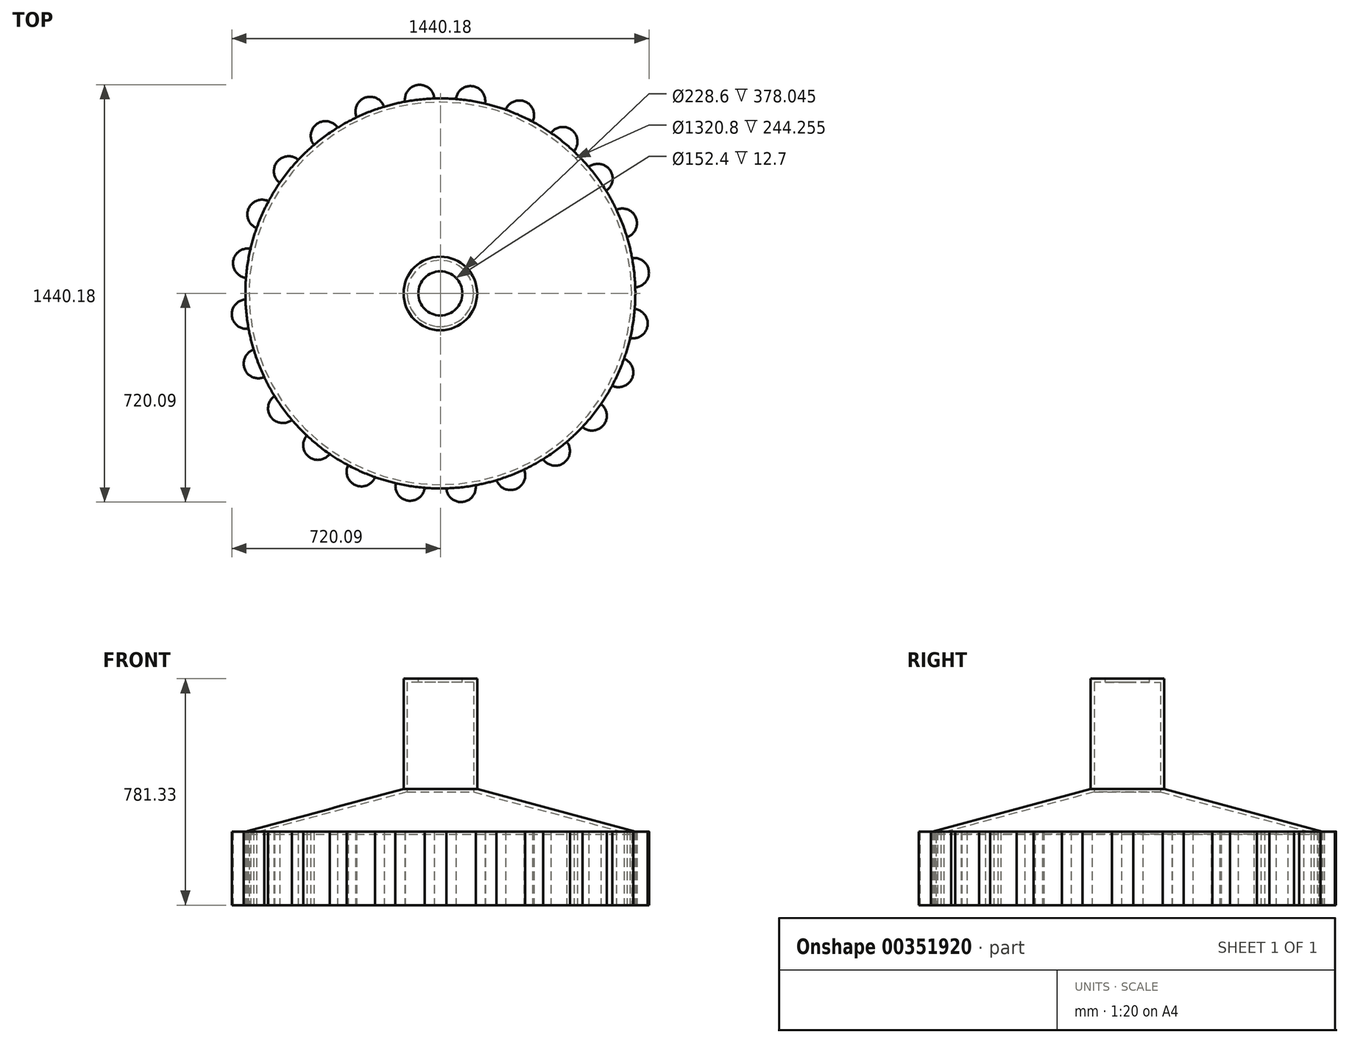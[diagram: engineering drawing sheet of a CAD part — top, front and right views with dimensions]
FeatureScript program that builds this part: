
annotation { "Feature Type Name" : "Feature", "Feature Type Description" : "" }
export const myFeature = defineFeature(function(context is Context, id is Id, definition is map)
    precondition{}
    {
        {
            var Q0;
            Q0=qCreatedBy(makeId("Front.planeOp"),FACE);
            var sketch = newSketch(context, id + "F0", { "sketchPlane" : qUnion([Q0])});
            skLineSegment(sketch, "E0", {"start": v(0, 0) * mm, "end": v(-673.1, 0) * mm});
            skLineSegment(sketch, "E1", {"start": v(-673.1, 0) * mm, "end": v(-673.1, 254) * mm});
            skLineSegment(sketch, "E2", {"start": v(-673.1, 254) * mm, "end": v(-127, 400.33) * mm});
            skPoint(sketch, "E3.center", {"position": v(0, 0) * mm});
            skLineSegment(sketch, "E4", {"start": v(0, 0) * mm, "end": v(0, 1146.38) * mm, "construction": true});
            skLineSegment(sketch, "E5", {"start": v(0, 0) * mm, "end": v(0, 781.33) * mm});
            skLineSegment(sketch, "E6", {"start": v(-127, 781.33) * mm, "end": v(0, 781.33) * mm});
            skLineSegment(sketch, "E7", {"start": v(-127, 400.33) * mm, "end": v(-127, 781.33) * mm});
            skSolve(sketch);
        }
        {
            var Q0;
            Q0=makeQuery(id+"F0.imprint","IMPRINT",FACE,{"disambiguationData":[TD([[makeQuery(id+"F0.imprint","IMPRINT",EDGE,{"derivedFrom":sQuery(id+"F0.wireOp",EDGE,"E0")}),-1.0]])]});
            var Q1;
            Q1=sQuery(id+"F0.wireOp",EDGE,"E4");
            revolve(context, id + "F1", {"entities" : qUnion([Q0]), "axis" : qUnion([Q1]), "revolveType" : RevolveType.FULL});
        }
        {
            var Q0;
            Q0=makeQuery(id+"F1.opRevolve","SWEPT_FACE",FACE,{"disambiguationData":[OSD([sQuery(id+"F0.wireOp",EDGE,"E0")])]});
            shell(context, id + "F2", {"entities" : qUnion([Q0]), "thickness" : 12.7 * mm});
        }
        {
            var Q0;
            Q0=makeQuery(id+"F1.opRevolve","SWEPT_FACE",FACE,{"disambiguationData":[OSD([sQuery(id+"F0.wireOp",EDGE,"E6")])]});
            var sketch = newSketch(context, id + "F3", { "sketchPlane" : qUnion([Q0])});
            skCircle(sketch, "E8", {"center": v(0, 0) * mm, "radius": 76.2 * mm});
            skSolve(sketch);
        }
        {
            var Q0;
            Q0=qSketchRegion(id+"F3",true);
            extrude(context, id + "F4", {"entities" : qUnion([Q0]), "operationType" : NewBodyOperationType.REMOVE, "endBound" : BoundingType.THROUGH_ALL, "oppositeDirection" : true, "depth" : 25.4 * mm});
        }
        {
            var Q0;
            Q0=makeQuery(id+"F1.opRevolve","SWEPT_FACE",FACE,{"disambiguationData":[OSD([sQuery(id+"F0.wireOp",EDGE,"E0")])]});
            var sketch = newSketch(context, id + "F5", { "sketchPlane" : qUnion([Q0])});
            skArc(sketch, "E9", {"start": v(-607.93, 288.94) * mm, "mid": v(-675.38, 260.55) * mm, "end": v(-644.47, 194.22) * mm});
            skArc(sketch, "E10", {"start": v(-607.93, 288.94) * mm, "mid": v(-627.99, 242.27) * mm, "end": v(-644.47, 194.22) * mm});
            skSolve(sketch);
        }
        {
            var Q0;
            Q0=makeQuery(id+"F5.imprint","IMPRINT",FACE,{"disambiguationData":[TD([[makeQuery(id+"F5.imprint","IMPRINT",EDGE,{"derivedFrom":sQuery(id+"F5.wireOp",EDGE,"E9")}),1.0]])]});
            extrude(context, id + "F6", {"entities" : qUnion([Q0]), "oppositeDirection" : true, "depth" : 254 * mm});
        }
        {
            var Q0;
            Q0=makeQuery(id+"F6.opExtrude","SWEPT_BODY",BODY,{"disambiguationData":[OSD([sQuery(id+"F5.wireOp",EDGE,"E9"),sQuery(id+"F5.wireOp",EDGE,"E10")])]});
            var Q1;
            Q1=makeQuery(id+"F4.boolean.opBoolean","INTERSECT",EDGE,{"derivedFrom":[makeQuery(id+"F2.opShell","OFFSET_FACE",FACE,{"disambiguationData":[OSD([sQuery(id+"F0.wireOp",EDGE,"E6")])]}),makeQuery(id+"F4.opExtrude","SWEPT_FACE",FACE,{"disambiguationData":[OSD([sQuery(id+"F3.wireOp",EDGE,"E8")])]})]});
            circularPattern(context, id + "F7", {"operationType" : NewBodyOperationType.ADD, "entities" : qUnion([Q0]), "axis" : qUnion([Q1]), "angle" : 360 * degree, "instanceCount" : 24, "equalSpace" : true});
        }
    });
